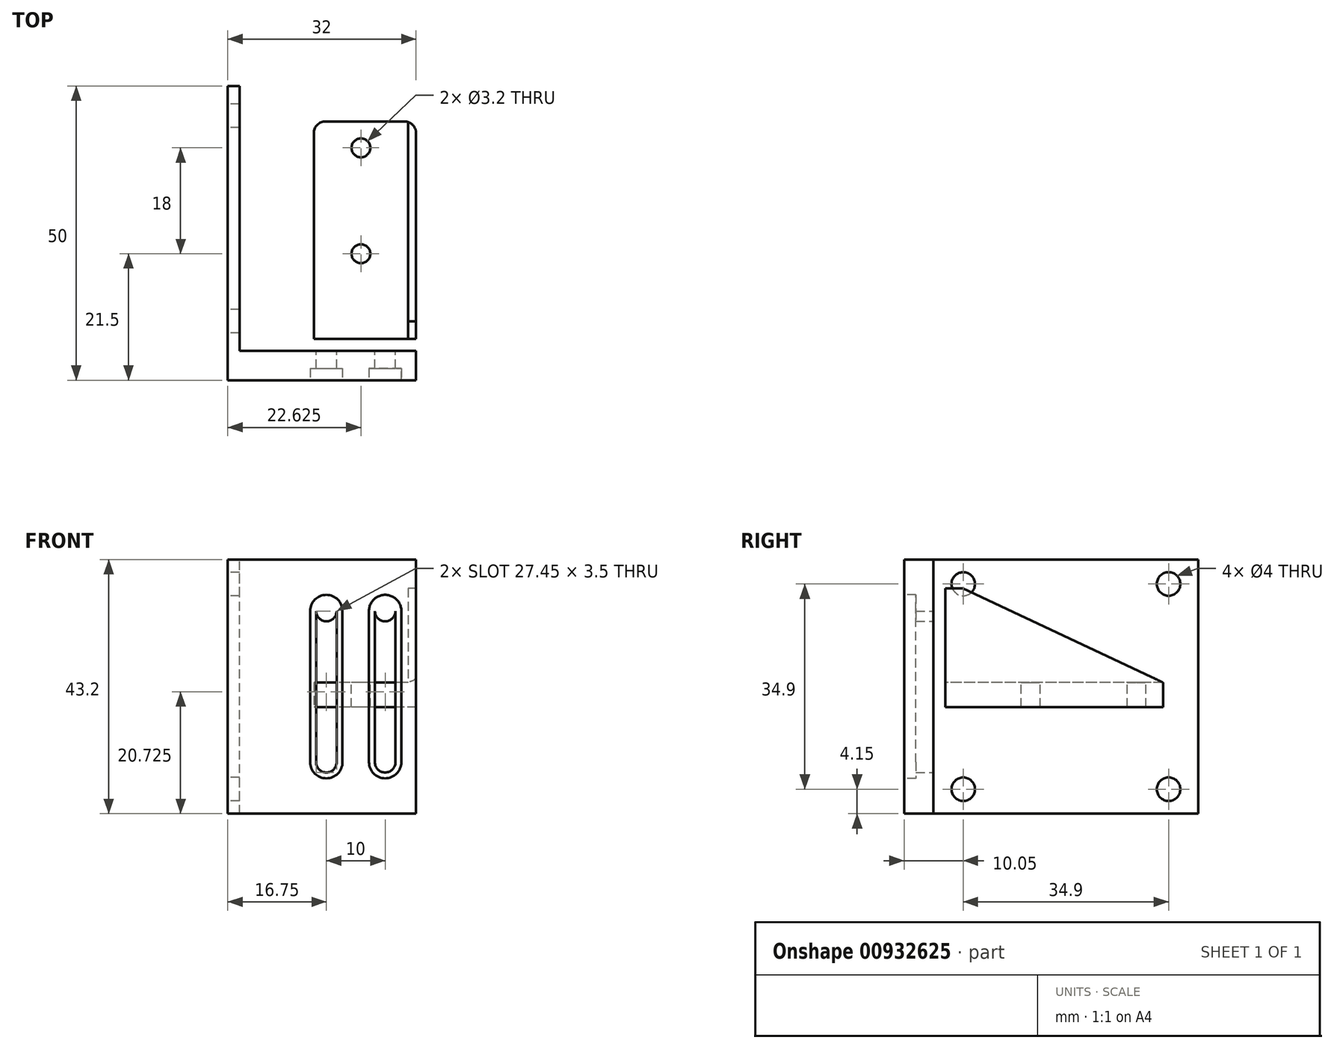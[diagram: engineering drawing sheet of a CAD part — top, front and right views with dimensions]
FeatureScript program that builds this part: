
annotation { "Feature Type Name" : "Feature", "Feature Type Description" : "" }
export const myFeature = defineFeature(function(context is Context, id is Id, definition is map)
    precondition{}
    {
        {
            var Q0;
            Q0=qCreatedBy(makeId("Right.planeOp"),FACE);
            var sketch = newSketch(context, id + "F0", { "sketchPlane" : qUnion([Q0])});
            skLineSegment(sketch, "E0.bottom", {"start": v(25, -21.6) * mm, "end": v(-25, -21.6) * mm});
            skLineSegment(sketch, "E0.top", {"start": v(25, 21.6) * mm, "end": v(-25, 21.6) * mm});
            skLineSegment(sketch, "E0.left", {"start": v(25, -21.6) * mm, "end": v(25, 21.6) * mm});
            skLineSegment(sketch, "E0.right", {"start": v(-25, -21.6) * mm, "end": v(-25, 21.6) * mm});
            skPoint(sketch, "E0.middle", {"position": v(0, 0) * mm});
            skLineSegment(sketch, "E1", {"start": v(-20, 0) * mm, "end": v(-20, -21.6) * mm});
            skLineSegment(sketch, "E2", {"start": v(-20, 0) * mm, "end": v(-20, 21.6) * mm});
            skCircle(sketch, "E3", {"center": v(-14.95, 17.45) * mm, "radius": 2 * mm});
            skCircle(sketch, "E4", {"center": v(19.95, 17.45) * mm, "radius": 2 * mm});
            skCircle(sketch, "E5", {"center": v(-14.95, -17.45) * mm, "radius": 2 * mm});
            skCircle(sketch, "E6", {"center": v(19.95, -17.45) * mm, "radius": 2 * mm});
            skPoint(sketch, "E7.endSnap0", {"position": v(-20, -10.8) * mm});
            skSolve(sketch);
        }
        {
            var Q0;
            {var subQ0=sQuery(id+"F0.wireOp",EDGE,"E0.left");Q0=makeQuery(id+"F0.imprint","IMPRINT",FACE,{"disambiguationData":[TD([[makeQuery(id+"F0.imprint","IMPRINT",EDGE,{"derivedFrom":subQ0}),1.0]])]});}
            extrude(context, id + "F1", {"entities" : qUnion([Q0]), "depth" : 2 * mm, "offsetDistance" : 25 * mm});
        }
        {
            var Q0;
            {var subQ0=sQuery(id+"F0.wireOp",EDGE,"E0.right");Q0=makeQuery(id+"F0.imprint","IMPRINT",FACE,{"disambiguationData":[TD([[makeQuery(id+"F0.imprint","IMPRINT",EDGE,{"derivedFrom":subQ0}),-1.0]])]});}
            extrude(context, id + "F2", {"entities" : qUnion([Q0]), "operationType" : NewBodyOperationType.ADD, "depth" : 32 * mm, "offsetDistance" : 25 * mm});
        }
        {
            var Q0;
            Q0=makeQuery(id+"F2.opExtrude","SWEPT_FACE",FACE,{"disambiguationData":[OSD([sQuery(id+"F0.wireOp",EDGE,"E1"),sQuery(id+"F0.wireOp",EDGE,"E2")])]});
            var sketch = newSketch(context, id + "F3", { "sketchPlane" : qUnion([Q0])});
            skCircle(sketch, "E8", {"center": v(-26.75, 12.85) * mm, "radius": 1.75 * mm});
            skCircle(sketch, "E9", {"center": v(-26.75, -12.85) * mm, "radius": 1.75 * mm});
            skCircle(sketch, "E10", {"center": v(-16.75, 12.85) * mm, "radius": 1.75 * mm});
            skCircle(sketch, "E11", {"center": v(-16.75, -12.85) * mm, "radius": 1.75 * mm});
            skLineSegment(sketch, "E12", {"start": v(-28.5, 12.85) * mm, "end": v(-28.5, -12.85) * mm});
            skLineSegment(sketch, "E13", {"start": v(-25, 12.85) * mm, "end": v(-25, -12.85) * mm});
            skLineSegment(sketch, "E14", {"start": v(-18.5, 12.85) * mm, "end": v(-18.5, -12.85) * mm});
            skLineSegment(sketch, "E15", {"start": v(-15, 12.85) * mm, "end": v(-15, -12.85) * mm});
            skSolve(sketch);
        }
        {
            var Q0;
            {var subQ0=sQuery(id+"F3.wireOp",EDGE,"E12");Q0=makeQuery(id+"F3.imprint","IMPRINT",FACE,{"disambiguationData":[TD([[makeQuery(id+"F3.imprint","IMPRINT",EDGE,{"derivedFrom":subQ0}),1.0]])]});}
            var Q1;
            {var subQ0=sQuery(id+"F3.wireOp",EDGE,"E8");var subQ2=makeQuery(id+"F3.imprint","IMPRINT",VERTEX,{"derivedFrom":subQ0});Q1=makeQuery(id+"F3.imprint","IMPRINT",FACE,{"disambiguationData":[TD([[makeQuery(id+"F3.imprint","IMPRINT",EDGE,{"disambiguationData":[TD([[subQ2,1.0]])],"derivedFrom":subQ0}),1.0]])]});}
            var Q2;
            {var subQ0=sQuery(id+"F3.wireOp",EDGE,"E9");var subQ1=makeQuery(id+"F3.imprint","INTERSECT",VERTEX,{"derivedFrom":[subQ0,sQuery(id+"F3.wireOp",EDGE,"E12")]});Q2=makeQuery(id+"F3.imprint","IMPRINT",FACE,{"disambiguationData":[TD([[makeQuery(id+"F3.imprint","IMPRINT",EDGE,{"disambiguationData":[TD([[subQ1,1.0]])],"derivedFrom":subQ0}),1.0]])]});}
            var Q3;
            {var subQ0=sQuery(id+"F3.wireOp",EDGE,"E14");Q3=makeQuery(id+"F3.imprint","IMPRINT",FACE,{"disambiguationData":[TD([[makeQuery(id+"F3.imprint","IMPRINT",EDGE,{"derivedFrom":subQ0}),1.0]])]});}
            var Q4;
            {var subQ0=sQuery(id+"F3.wireOp",EDGE,"E11");var subQ1=makeQuery(id+"F3.imprint","INTERSECT",VERTEX,{"derivedFrom":[subQ0,sQuery(id+"F3.wireOp",EDGE,"E14")]});Q4=makeQuery(id+"F3.imprint","IMPRINT",FACE,{"disambiguationData":[TD([[makeQuery(id+"F3.imprint","IMPRINT",EDGE,{"disambiguationData":[TD([[subQ1,1.0]])],"derivedFrom":subQ0}),1.0]])]});}
            var Q5;
            {var subQ0=sQuery(id+"F3.wireOp",EDGE,"E10");var subQ2=makeQuery(id+"F3.imprint","IMPRINT",VERTEX,{"derivedFrom":subQ0});Q5=makeQuery(id+"F3.imprint","IMPRINT",FACE,{"disambiguationData":[TD([[makeQuery(id+"F3.imprint","IMPRINT",EDGE,{"disambiguationData":[TD([[subQ2,1.0]])],"derivedFrom":subQ0}),1.0]])]});}
            extrude(context, id + "F4", {"entities" : qUnion([Q0, Q1, Q2, Q3, Q4, Q5]), "operationType" : NewBodyOperationType.REMOVE, "oppositeDirection" : true, "depth" : 25 * mm, "offsetDistance" : 25 * mm});
        }
        {
            var Q0;
            Q0=makeQuery(id+"F2.opExtrude","SWEPT_FACE",FACE,{"disambiguationData":[OSD([sQuery(id+"F0.wireOp",EDGE,"E0.right")])]});
            var sketch = newSketch(context, id + "F5", { "sketchPlane" : qUnion([Q0])});
            skArc(sketch, "E16.0", {"start": v(14, -12.85) * mm, "mid": v(16.75, -15.6) * mm, "end": v(19.5, -12.85) * mm});
            skLineSegment(sketch, "E16.1", {"start": v(14, -12.85) * mm, "end": v(14, 12.85) * mm});
            skArc(sketch, "E16.2", {"start": v(19.5, 12.85) * mm, "mid": v(16.75, 15.6) * mm, "end": v(14, 12.85) * mm});
            skLineSegment(sketch, "E16.3", {"start": v(19.5, -12.85) * mm, "end": v(19.5, 12.85) * mm});
            skLineSegment(sketch, "E17.0", {"start": v(29.5, -12.85) * mm, "end": v(29.5, 12.85) * mm});
            skArc(sketch, "E17.1", {"start": v(24, -12.85) * mm, "mid": v(26.75, -15.6) * mm, "end": v(29.5, -12.85) * mm});
            skLineSegment(sketch, "E17.2", {"start": v(24, -12.85) * mm, "end": v(24, 12.82) * mm});
            skArc(sketch, "E18.2", {"start": v(29.5, 12.85) * mm, "mid": v(26.74, 15.6) * mm, "end": v(24, 12.82) * mm});
            skSolve(sketch);
        }
        {
            var Q0;
            Q0=makeQuery(id+"F5.imprint","IMPRINT",FACE,{"disambiguationData":[TD([[makeQuery(id+"F5.imprint","IMPRINT",EDGE,{"derivedFrom":sQuery(id+"F5.wireOp",EDGE,"E16.0")}),1.0]])]});
            var Q1;
            Q1=makeQuery(id+"F5.imprint","IMPRINT",FACE,{"disambiguationData":[TD([[makeQuery(id+"F5.imprint","IMPRINT",EDGE,{"derivedFrom":sQuery(id+"F5.wireOp",EDGE,"E17.0")}),1.0]])]});
            extrude(context, id + "F6", {"entities" : qUnion([Q0, Q1]), "operationType" : NewBodyOperationType.REMOVE, "oppositeDirection" : true, "depth" : 2 * mm, "offsetDistance" : 25 * mm});
        }
        {
            var Q0;
            Q0=makeQuery(id+"F2.opExtrude","SWEPT_FACE",FACE,{"disambiguationData":[OSD([sQuery(id+"F0.wireOp",EDGE,"E1"),sQuery(id+"F0.wireOp",EDGE,"E2")])]});
            cPlane(context, id + "F7", {"entities" : qUnion([Q0]), "cplaneType" : CPlaneType.OFFSET, "offset" : 2 * mm, "width" : 150 * mm, "height" : 150 * mm});
        }
        {
            var Q0;
            Q0=qCreatedBy(id+"F7.planeOp",FACE);
            var sketch = newSketch(context, id + "F8", { "sketchPlane" : qUnion([Q0])});
            skLineSegment(sketch, "E19.bottom", {"start": v(-30.63, 16.7) * mm, "end": v(-14.63, 16.7) * mm});
            skLineSegment(sketch, "E19.top", {"start": v(-30.63, 0.7) * mm, "end": v(-14.63, 0.7) * mm});
            skLineSegment(sketch, "E19.left", {"start": v(-30.63, 16.7) * mm, "end": v(-30.63, 0.7) * mm});
            skLineSegment(sketch, "E19.right", {"start": v(-14.63, 16.7) * mm, "end": v(-14.63, 0.7) * mm});
            skLineSegment(sketch, "E20.top", {"start": v(-30.63, -3.5) * mm, "end": v(-14.63, -3.5) * mm});
            skLineSegment(sketch, "E20.left", {"start": v(-30.63, 0.7) * mm, "end": v(-30.63, -3.5) * mm});
            skLineSegment(sketch, "E20.right", {"start": v(-14.63, 0.7) * mm, "end": v(-14.63, -3.5) * mm});
            skLineSegment(sketch, "E21.bottom", {"start": v(-30.63, -3.5) * mm, "end": v(-32, -3.5) * mm});
            skLineSegment(sketch, "E21.top", {"start": v(-30.63, 16.7) * mm, "end": v(-32, 16.7) * mm});
            skLineSegment(sketch, "E21.left", {"start": v(-30.63, -3.5) * mm, "end": v(-30.63, 16.7) * mm});
            skLineSegment(sketch, "E21.right", {"start": v(-32, -3.5) * mm, "end": v(-32, 16.7) * mm});
            skLineSegment(sketch, "E22.bottom", {"start": v(-19.48, 14.6) * mm, "end": v(-19.28, 14.6) * mm});
            skLineSegment(sketch, "E22.top", {"start": v(-19.48, 2.55) * mm, "end": v(-19.28, 2.55) * mm});
            skLineSegment(sketch, "E22.left", {"start": v(-20.88, 13) * mm, "end": v(-20.88, 4.15) * mm});
            skLineSegment(sketch, "E22.right", {"start": v(-17.88, 13) * mm, "end": v(-17.88, 4.15) * mm});
            skPoint(sketch, "E23.visualSharp", {"position": v(-20.88, 14.6) * mm});
            skArc(sketch, "E23.filletArc", {"start": v(-19.28, 14.6) * mm, "mid": v(-20.4, 14.13) * mm, "end": v(-20.88, 13) * mm});
            skPoint(sketch, "E24.visualSharp", {"position": v(-20.88, 2.55) * mm});
            skArc(sketch, "E24.filletArc", {"start": v(-20.88, 4.15) * mm, "mid": v(-20.4, 3.02) * mm, "end": v(-19.28, 2.55) * mm});
            skPoint(sketch, "E25.visualSharp", {"position": v(-17.88, 2.55) * mm});
            skArc(sketch, "E25.filletArc", {"start": v(-19.48, 2.55) * mm, "mid": v(-18.34, 3.02) * mm, "end": v(-17.88, 4.15) * mm});
            skPoint(sketch, "E26.visualSharp", {"position": v(-17.88, 14.6) * mm});
            skArc(sketch, "E26.filletArc", {"start": v(-17.88, 13) * mm, "mid": v(-18.34, 14.13) * mm, "end": v(-19.48, 14.6) * mm});
            skSolve(sketch);
        }
        {
            var Q0;
            Q0=makeQuery(id+"F8.imprint","IMPRINT",FACE,{"disambiguationData":[TD([[makeQuery(id+"F8.imprint","IMPRINT",EDGE,{"derivedFrom":sQuery(id+"F8.wireOp",EDGE,"E20.top")}),1.0]])]});
            var Q1;
            {var subQ3=sQuery(id+"F8.wireOp",EDGE,"E21.bottom");Q1=makeQuery(id+"F8.imprint","IMPRINT",FACE,{"disambiguationData":[TD([[makeQuery(id+"F8.imprint","IMPRINT",EDGE,{"derivedFrom":subQ3}),-1.0]])]});}
            extrude(context, id + "F9", {"entities" : qUnion([Q0, Q1]), "depth" : 37 * mm, "offsetDistance" : 25 * mm});
        }
        {
            var Q0;
            Q0=makeQuery(id+"F9.opExtrude","CAP_EDGE",EDGE,{"disambiguationData":[OSD([sQuery(id+"F8.wireOp",EDGE,"E21.top")])],"isStart":false});
            chamfer(context, id + "F10", {"entities" : qUnion([Q0]), "chamferType" : ChamferType.TWO_OFFSETS, "width1" : 16 * mm, "oppositeDirection" : false, "width2" : 34 * mm, "tangentPropagation" : true});
        }
        {
            var Q0;
            Q0=makeQuery(id+"F9.opExtrude","SWEPT_FACE",FACE,{"disambiguationData":[OSD([sQuery(id+"F8.wireOp",EDGE,"E19.top")])]});
            var sketch = newSketch(context, id + "F11", { "sketchPlane" : qUnion([Q0])});
            skCircle(sketch, "E27", {"center": v(22.63, -3.5) * mm, "radius": 1.6 * mm});
            skCircle(sketch, "E28", {"center": v(22.63, 14.5) * mm, "radius": 1.6 * mm});
            skSolve(sketch);
        }
        {
            var Q0;
            Q0=makeQuery(id+"F11.imprint","IMPRINT",FACE,{"disambiguationData":[TD([[makeQuery(id+"F11.imprint","IMPRINT",EDGE,{"derivedFrom":sQuery(id+"F11.wireOp",EDGE,"E27")}),1.0]])]});
            var Q1;
            Q1=makeQuery(id+"F11.imprint","IMPRINT",FACE,{"disambiguationData":[TD([[makeQuery(id+"F11.imprint","IMPRINT",EDGE,{"derivedFrom":sQuery(id+"F11.wireOp",EDGE,"E28")}),1.0]])]});
            extrude(context, id + "F12", {"entities" : qUnion([Q0, Q1]), "operationType" : NewBodyOperationType.REMOVE, "oppositeDirection" : true, "depth" : 5 * mm, "offsetDistance" : 25 * mm});
        }
        {
            var Q0;
            Q0=makeQuery(id+"F9.opExtrude","CAP_EDGE",EDGE,{"disambiguationData":[OSD([sQuery(id+"F8.wireOp",EDGE,"E20.right")])],"isStart":false});
            var Q1;
            Q1=makeQuery(id+"F9.opExtrude","CAP_EDGE",EDGE,{"disambiguationData":[OSD([sQuery(id+"F8.wireOp",EDGE,"E21.right")])],"isStart":false});
            fillet(context, id + "F13", {"entities" : qUnion([Q0, Q1]), "radius" : 2 * mm, "tangentPropagation" : true, "allowEdgeOverflow" : false});
        }
    });
